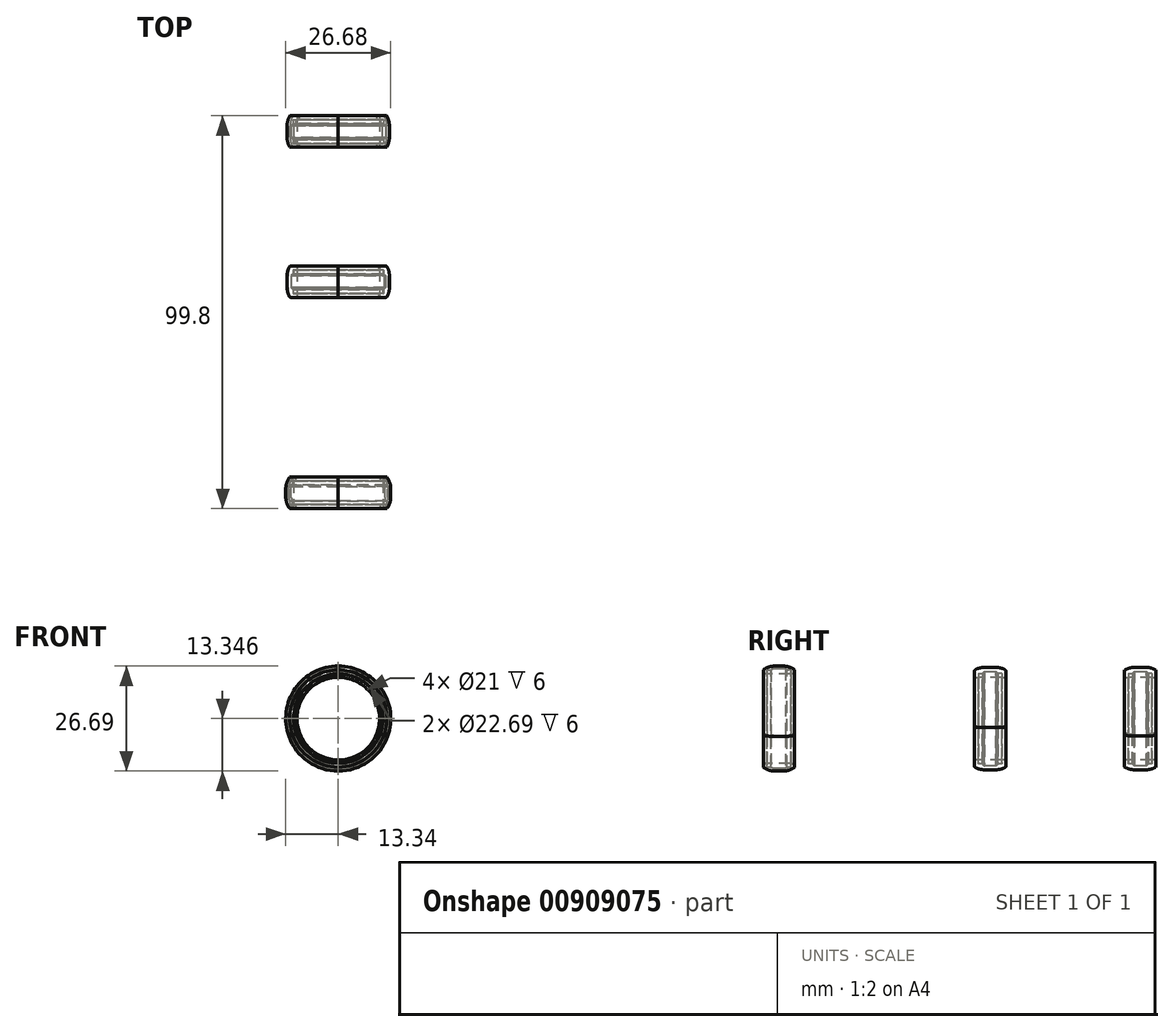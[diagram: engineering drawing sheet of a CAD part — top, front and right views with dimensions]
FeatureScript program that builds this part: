
annotation { "Feature Type Name" : "Feature", "Feature Type Description" : "" }
export const myFeature = defineFeature(function(context is Context, id is Id, definition is map)
    precondition{}
    {
        {
            var Q0;
            Q0=qCreatedBy(makeId("Right.planeOp"),FACE);
            var sketch = newSketch(context, id + "F0", { "sketchPlane" : qUnion([Q0])});
            skLineSegment(sketch, "E0", {"start": v(-19.63, -18.34) * mm, "end": v(80.37, -18.34) * mm, "construction": true});
            skLineSegment(sketch, "E1", {"start": v(-43.65, -18.34) * mm, "end": v(56.35, -18.34) * mm, "construction": true});
            skLineSegment(sketch, "E2.left", {"start": v(-31.4, -5) * mm, "end": v(-31.4, -7) * mm});
            skLineSegment(sketch, "E2.right", {"start": v(-23.4, -5) * mm, "end": v(-23.4, -6) * mm});
            skLineSegment(sketch, "E3", {"start": v(-30.4, -6) * mm, "end": v(-29.4, -6) * mm});
            skLineSegment(sketch, "E4", {"start": v(-24.4, -6) * mm, "end": v(-25.4, -6) * mm});
            skLineSegment(sketch, "E5", {"start": v(-29.4, -6) * mm, "end": v(-29.05, -5.65) * mm});
            skLineSegment(sketch, "E6", {"start": v(-25.4, -6) * mm, "end": v(-25.75, -5.65) * mm});
            skLineSegment(sketch, "E7", {"start": v(-29.05, -5.65) * mm, "end": v(-25.75, -5.65) * mm});
            skArc(sketch, "E8", {"start": v(-23.4, -5) * mm, "mid": v(-27.4, -4.36) * mm, "end": v(-31.4, -5) * mm});
            skPoint(sketch, "E9", {"position": v(-27.4, -5) * mm});
            skLineSegment(sketch, "E10", {"start": v(-23.4, -6) * mm, "end": v(-23.4, -7) * mm});
            skLineSegment(sketch, "E11", {"start": v(-30.4, -6) * mm, "end": v(-30.4, -7) * mm});
            skLineSegment(sketch, "E12", {"start": v(-24.4, -6) * mm, "end": v(-24.4, -7) * mm});
            skLineSegment(sketch, "E13", {"start": v(-31.4, -5) * mm, "end": v(-23.4, -5) * mm});
            skLineSegment(sketch, "E14", {"start": v(-31.4, -7) * mm, "end": v(-30.4, -7) * mm});
            skLineSegment(sketch, "E15", {"start": v(-24.4, -7) * mm, "end": v(-23.4, -7) * mm});
            skLineSegment(sketch, "E16", {"start": v(-30.4, -7) * mm, "end": v(-24.4, -7) * mm});
            skLineSegment(sketch, "E17.left", {"start": v(60.4, -5.34) * mm, "end": v(60.4, -7.84) * mm});
            skLineSegment(sketch, "E17.right", {"start": v(68.4, -5.34) * mm, "end": v(68.4, -6.84) * mm});
            skLineSegment(sketch, "E18", {"start": v(61.4, -6.84) * mm, "end": v(62.4, -6.84) * mm});
            skLineSegment(sketch, "E19", {"start": v(67.4, -6.84) * mm, "end": v(66.4, -6.84) * mm});
            skLineSegment(sketch, "E20", {"start": v(62.4, -6.84) * mm, "end": v(62.9, -6.34) * mm});
            skLineSegment(sketch, "E21", {"start": v(66.4, -6.84) * mm, "end": v(65.9, -6.34) * mm});
            skLineSegment(sketch, "E22", {"start": v(62.9, -6.34) * mm, "end": v(65.9, -6.34) * mm});
            skArc(sketch, "E23", {"start": v(68.4, -5.34) * mm, "mid": v(64.4, -4.7) * mm, "end": v(60.4, -5.34) * mm});
            skPoint(sketch, "E24", {"position": v(64.4, -5.34) * mm});
            skLineSegment(sketch, "E25", {"start": v(68.4, -6.84) * mm, "end": v(68.4, -7.84) * mm});
            skLineSegment(sketch, "E26", {"start": v(61.4, -6.84) * mm, "end": v(61.4, -7.84) * mm});
            skLineSegment(sketch, "E27", {"start": v(67.4, -6.84) * mm, "end": v(67.4, -7.84) * mm});
            skLineSegment(sketch, "E28", {"start": v(60.4, -5.34) * mm, "end": v(68.4, -5.34) * mm});
            skLineSegment(sketch, "E29", {"start": v(60.4, -7.84) * mm, "end": v(61.4, -7.84) * mm});
            skLineSegment(sketch, "E30", {"start": v(67.4, -7.84) * mm, "end": v(68.4, -7.84) * mm});
            skLineSegment(sketch, "E31", {"start": v(61.4, -7.84) * mm, "end": v(67.4, -7.84) * mm});
            skLineSegment(sketch, "E32.left", {"start": v(-14.14, -5.7) * mm, "end": v(-14.14, -7.84) * mm});
            skLineSegment(sketch, "E32.right", {"start": v(-6.14, -5.7) * mm, "end": v(-6.14, -7.14) * mm});
            skLineSegment(sketch, "E33", {"start": v(-13.14, -7.14) * mm, "end": v(-12.14, -7.14) * mm});
            skLineSegment(sketch, "E34", {"start": v(-7.14, -7.14) * mm, "end": v(-8.14, -7.14) * mm});
            skLineSegment(sketch, "E35", {"start": v(-12.14, -7.14) * mm, "end": v(-11.4, -6.4) * mm});
            skLineSegment(sketch, "E36", {"start": v(-8.14, -7.14) * mm, "end": v(-8.9, -6.4) * mm});
            skLineSegment(sketch, "E37", {"start": v(-11.4, -6.4) * mm, "end": v(-8.9, -6.4) * mm});
            skPoint(sketch, "E38", {"position": v(-10.14, -5.7) * mm});
            skLineSegment(sketch, "E39", {"start": v(-6.14, -7.14) * mm, "end": v(-6.14, -7.84) * mm});
            skLineSegment(sketch, "E40", {"start": v(-13.14, -7.14) * mm, "end": v(-13.14, -7.84) * mm});
            skLineSegment(sketch, "E41", {"start": v(-7.14, -7.14) * mm, "end": v(-7.14, -7.84) * mm});
            skLineSegment(sketch, "E42", {"start": v(-14.14, -5.7) * mm, "end": v(-6.14, -5.7) * mm});
            skLineSegment(sketch, "E43", {"start": v(-14.14, -7.84) * mm, "end": v(-13.14, -7.84) * mm});
            skLineSegment(sketch, "E44", {"start": v(-7.14, -7.84) * mm, "end": v(-6.14, -7.84) * mm});
            skLineSegment(sketch, "E45", {"start": v(-13.14, -7.84) * mm, "end": v(-7.14, -7.84) * mm});
            skLineSegment(sketch, "E46.left", {"start": v(22.26, -5.34) * mm, "end": v(22.26, -7.84) * mm});
            skLineSegment(sketch, "E46.right", {"start": v(30.26, -5.34) * mm, "end": v(30.26, -6.84) * mm});
            skLineSegment(sketch, "E47", {"start": v(23.26, -6.84) * mm, "end": v(24.26, -6.84) * mm});
            skLineSegment(sketch, "E48", {"start": v(29.26, -6.84) * mm, "end": v(28.26, -6.84) * mm});
            skLineSegment(sketch, "E49", {"start": v(24.26, -6.84) * mm, "end": v(24.76, -6.34) * mm});
            skLineSegment(sketch, "E50", {"start": v(28.26, -6.84) * mm, "end": v(27.76, -6.34) * mm});
            skLineSegment(sketch, "E51", {"start": v(24.76, -6.34) * mm, "end": v(27.76, -6.34) * mm});
            skPoint(sketch, "E52", {"position": v(26.26, -5.34) * mm});
            skLineSegment(sketch, "E53", {"start": v(30.26, -6.84) * mm, "end": v(30.26, -7.84) * mm});
            skLineSegment(sketch, "E54", {"start": v(23.26, -6.84) * mm, "end": v(23.26, -7.84) * mm});
            skLineSegment(sketch, "E55", {"start": v(29.26, -6.84) * mm, "end": v(29.26, -7.84) * mm});
            skLineSegment(sketch, "E56", {"start": v(22.26, -5.34) * mm, "end": v(30.26, -5.34) * mm});
            skLineSegment(sketch, "E57", {"start": v(22.26, -7.84) * mm, "end": v(23.26, -7.84) * mm});
            skLineSegment(sketch, "E58", {"start": v(29.26, -7.84) * mm, "end": v(30.26, -7.84) * mm});
            skLineSegment(sketch, "E59", {"start": v(23.26, -7.84) * mm, "end": v(29.26, -7.84) * mm});
            skSolve(sketch);
        }
        {
            var Q0;
            Q0=makeQuery(id+"F0.imprint","IMPRINT",FACE,{"disambiguationData":[TD([[makeQuery(id+"F0.imprint","IMPRINT",EDGE,{"derivedFrom":sQuery(id+"F0.wireOp",EDGE,"E3")}),-1.0]])]});
            var Q1;
            Q1=sQuery(id+"F0.wireOp",EDGE,"E0");
            revolve(context, id + "F1", {"surfaceOperationType" : NewSurfaceOperationType.NEW, "entities" : qUnion([Q0]), "axis" : qUnion([Q1]), "revolveType" : RevolveType.FULL});
        }
        {
            var Q0;
            Q0=makeQuery(id+"F1.opRevolve","SWEPT_EDGE",EDGE,{"disambiguationData":[OSD([sQuery(id+"F0.wireOp",EDGE,"E5"),sQuery(id+"F0.wireOp",EDGE,"E7")])]});
            var Q1;
            Q1=makeQuery(id+"F1.opRevolve","SWEPT_EDGE",EDGE,{"disambiguationData":[OSD([sQuery(id+"F0.wireOp",EDGE,"E6"),sQuery(id+"F0.wireOp",EDGE,"E7")])]});
            fillet(context, id + "F2", {"entities" : qUnion([Q0, Q1]), "radius" : 1 * mm, "tangentPropagation" : true, "allowEdgeOverflow" : false});
        }
        {
            var Q0;
            Q0=makeQuery(id+"F0.imprint","IMPRINT",FACE,{"disambiguationData":[TD([[makeQuery(id+"F0.imprint","IMPRINT",EDGE,{"derivedFrom":sQuery(id+"F0.wireOp",EDGE,"E2.left")}),1.0]])]});
            var Q1;
            Q1=makeQuery(id+"F0.imprint","IMPRINT",FACE,{"disambiguationData":[TD([[makeQuery(id+"F0.imprint","IMPRINT",EDGE,{"derivedFrom":sQuery(id+"F0.wireOp",EDGE,"E17.left")}),1.0]])]});
            var Q2;
            Q2=sQuery(id+"F0.wireOp",EDGE,"E0");
            revolve(context, id + "F3", {"surfaceOperationType" : NewSurfaceOperationType.NEW, "entities" : qUnion([Q0, Q1]), "axis" : qUnion([Q2]), "revolveType" : RevolveType.ONE_DIRECTION, "angle" : 110 * degree});
        }
        {
            var Q0;
            Q0=makeQuery(id+"F3.opRevolve","SWEPT_EDGE",EDGE,{"disambiguationData":[OSD([sQuery(id+"F0.wireOp",EDGE,"E4"),sQuery(id+"F0.wireOp",EDGE,"E6")])]});
            var Q1;
            Q1=makeQuery(id+"F3.opRevolve","SWEPT_EDGE",EDGE,{"disambiguationData":[OSD([sQuery(id+"F0.wireOp",EDGE,"E5"),sQuery(id+"F0.wireOp",EDGE,"E7")])]});
            var Q2;
            Q2=makeQuery(id+"F3.opRevolve","SWEPT_EDGE",EDGE,{"disambiguationData":[OSD([sQuery(id+"F0.wireOp",EDGE,"E2.left"),sQuery(id+"F0.wireOp",EDGE,"E14")])]});
            var Q3;
            Q3=makeQuery(id+"F3.opRevolve","SWEPT_EDGE",EDGE,{"disambiguationData":[OSD([sQuery(id+"F0.wireOp",EDGE,"E10"),sQuery(id+"F0.wireOp",EDGE,"E15")])]});
            fillet(context, id + "F4", {"entities" : qUnion([Q0, Q1, Q2, Q3]), "radius" : 1 * mm, "tangentPropagation" : true, "allowEdgeOverflow" : false});
        }
        {
            var Q0;
            Q0=makeQuery(id+"F0.imprint","IMPRINT",FACE,{"disambiguationData":[TD([[makeQuery(id+"F0.imprint","IMPRINT",EDGE,{"derivedFrom":sQuery(id+"F0.wireOp",EDGE,"E2.left")}),1.0]])]});
            var Q1;
            Q1=makeQuery(id+"F0.imprint","IMPRINT",FACE,{"disambiguationData":[TD([[makeQuery(id+"F0.imprint","IMPRINT",EDGE,{"derivedFrom":sQuery(id+"F0.wireOp",EDGE,"E17.left")}),1.0]])]});
            var Q2;
            Q2=sQuery(id+"F0.wireOp",EDGE,"E0");
            revolve(context, id + "F5", {"surfaceOperationType" : NewSurfaceOperationType.NEW, "entities" : qUnion([Q0, Q1]), "axis" : qUnion([Q2]), "revolveType" : RevolveType.TWO_DIRECTIONS, "angle" : 250 * degree, "angleBack" : 110 * degree});
        }
        {
            var Q0;
            Q0=makeQuery(id+"F5.opRevolve","SWEPT_EDGE",EDGE,{"disambiguationData":[OSD([sQuery(id+"F0.wireOp",EDGE,"E4"),sQuery(id+"F0.wireOp",EDGE,"E6")])]});
            var Q1;
            Q1=makeQuery(id+"F5.opRevolve","SWEPT_EDGE",EDGE,{"disambiguationData":[OSD([sQuery(id+"F0.wireOp",EDGE,"E10"),sQuery(id+"F0.wireOp",EDGE,"E15")])]});
            var Q2;
            Q2=makeQuery(id+"F5.opRevolve","SWEPT_EDGE",EDGE,{"disambiguationData":[OSD([sQuery(id+"F0.wireOp",EDGE,"E2.left"),sQuery(id+"F0.wireOp",EDGE,"E14")])]});
            var Q3;
            Q3=makeQuery(id+"F5.opRevolve","SWEPT_EDGE",EDGE,{"disambiguationData":[OSD([sQuery(id+"F0.wireOp",EDGE,"E5"),sQuery(id+"F0.wireOp",EDGE,"E7")])]});
            fillet(context, id + "F6", {"entities" : qUnion([Q0, Q1, Q2, Q3]), "radius" : 1 * mm, "tangentPropagation" : true, "allowEdgeOverflow" : false});
        }
        {
            var Q0;
            Q0=makeQuery(id+"F0.imprint","IMPRINT",FACE,{"disambiguationData":[TD([[makeQuery(id+"F0.imprint","IMPRINT",EDGE,{"derivedFrom":sQuery(id+"F0.wireOp",EDGE,"E2.left")}),1.0]])]});
            var Q1;
            Q1=makeQuery(id+"F0.imprint","IMPRINT",FACE,{"disambiguationData":[TD([[makeQuery(id+"F0.imprint","IMPRINT",EDGE,{"derivedFrom":sQuery(id+"F0.wireOp",EDGE,"E17.left")}),1.0]])]});
            var Q2;
            Q2=sQuery(id+"F0.wireOp",EDGE,"E0");
            revolve(context, id + "F7", {"surfaceOperationType" : NewSurfaceOperationType.NEW, "entities" : qUnion([Q0, Q1]), "axis" : qUnion([Q2]), "revolveType" : RevolveType.TWO_DIRECTIONS, "angle" : 360 * degree, "angleBack" : 250 * degree});
        }
        {
            var Q0;
            Q0=makeQuery(id+"F7.opRevolve","SWEPT_EDGE",EDGE,{"disambiguationData":[OSD([sQuery(id+"F0.wireOp",EDGE,"E5"),sQuery(id+"F0.wireOp",EDGE,"E7")])]});
            var Q1;
            Q1=makeQuery(id+"F7.opRevolve","SWEPT_EDGE",EDGE,{"disambiguationData":[OSD([sQuery(id+"F0.wireOp",EDGE,"E2.left"),sQuery(id+"F0.wireOp",EDGE,"E14")])]});
            var Q2;
            Q2=makeQuery(id+"F7.opRevolve","SWEPT_EDGE",EDGE,{"disambiguationData":[OSD([sQuery(id+"F0.wireOp",EDGE,"E10"),sQuery(id+"F0.wireOp",EDGE,"E15")])]});
            var Q3;
            Q3=makeQuery(id+"F7.opRevolve","SWEPT_EDGE",EDGE,{"disambiguationData":[OSD([sQuery(id+"F0.wireOp",EDGE,"E4"),sQuery(id+"F0.wireOp",EDGE,"E6")])]});
            fillet(context, id + "F8", {"entities" : qUnion([Q0, Q1, Q2, Q3]), "radius" : 1 * mm, "tangentPropagation" : true, "allowEdgeOverflow" : false});
        }
        {
            var Q0;
            Q0=makeQuery(id+"F5.opRevolve","SWEPT_EDGE",EDGE,{"disambiguationData":[OSD([sQuery(id+"F0.wireOp",EDGE,"E2.right"),sQuery(id+"F0.wireOp",EDGE,"E8"),sQuery(id+"F0.wireOp",EDGE,"E13")])]});
            var Q1;
            Q1=makeQuery(id+"F5.opRevolve","SWEPT_EDGE",EDGE,{"disambiguationData":[OSD([sQuery(id+"F0.wireOp",EDGE,"E2.left"),sQuery(id+"F0.wireOp",EDGE,"E8"),sQuery(id+"F0.wireOp",EDGE,"E13")])]});
            var Q2;
            Q2=makeQuery(id+"F7.opRevolve","SWEPT_EDGE",EDGE,{"disambiguationData":[OSD([sQuery(id+"F0.wireOp",EDGE,"E2.left"),sQuery(id+"F0.wireOp",EDGE,"E8"),sQuery(id+"F0.wireOp",EDGE,"E13")])]});
            var Q3;
            Q3=makeQuery(id+"F7.opRevolve","SWEPT_EDGE",EDGE,{"disambiguationData":[OSD([sQuery(id+"F0.wireOp",EDGE,"E2.right"),sQuery(id+"F0.wireOp",EDGE,"E8"),sQuery(id+"F0.wireOp",EDGE,"E13")])]});
            var Q4;
            Q4=makeQuery(id+"F3.opRevolve","SWEPT_EDGE",EDGE,{"disambiguationData":[OSD([sQuery(id+"F0.wireOp",EDGE,"E2.right"),sQuery(id+"F0.wireOp",EDGE,"E8"),sQuery(id+"F0.wireOp",EDGE,"E13")])]});
            var Q5;
            Q5=makeQuery(id+"F3.opRevolve","SWEPT_EDGE",EDGE,{"disambiguationData":[OSD([sQuery(id+"F0.wireOp",EDGE,"E2.left"),sQuery(id+"F0.wireOp",EDGE,"E8"),sQuery(id+"F0.wireOp",EDGE,"E13")])]});
            fillet(context, id + "F9", {"entities" : qUnion([Q0, Q1, Q2, Q3, Q4, Q5]), "radius" : 5 * mm, "tangentPropagation" : true, "allowEdgeOverflow" : false});
        }
        {
            var Q0;
            Q0=makeQuery(id+"F0.imprint","IMPRINT",FACE,{"disambiguationData":[TD([[makeQuery(id+"F0.imprint","IMPRINT",EDGE,{"derivedFrom":sQuery(id+"F0.wireOp",EDGE,"E18")}),-1.0]])]});
            var Q1;
            Q1=sQuery(id+"F0.wireOp",EDGE,"E1");
            revolve(context, id + "F10", {"surfaceOperationType" : NewSurfaceOperationType.NEW, "entities" : qUnion([Q0]), "axis" : qUnion([Q1]), "revolveType" : RevolveType.FULL});
        }
        {
            var Q0;
            Q0=makeQuery(id+"F3.opRevolve","SWEPT_EDGE",EDGE,{"disambiguationData":[OSD([sQuery(id+"F0.wireOp",EDGE,"E17.right"),sQuery(id+"F0.wireOp",EDGE,"E23"),sQuery(id+"F0.wireOp",EDGE,"E28")])]});
            var Q1;
            Q1=makeQuery(id+"F3.opRevolve","SWEPT_EDGE",EDGE,{"disambiguationData":[OSD([sQuery(id+"F0.wireOp",EDGE,"E17.left"),sQuery(id+"F0.wireOp",EDGE,"E23"),sQuery(id+"F0.wireOp",EDGE,"E28")])]});
            var Q2;
            Q2=makeQuery(id+"F5.opRevolve","SWEPT_EDGE",EDGE,{"disambiguationData":[OSD([sQuery(id+"F0.wireOp",EDGE,"E17.left"),sQuery(id+"F0.wireOp",EDGE,"E23"),sQuery(id+"F0.wireOp",EDGE,"E28")])]});
            var Q3;
            Q3=makeQuery(id+"F7.opRevolve","SWEPT_EDGE",EDGE,{"disambiguationData":[OSD([sQuery(id+"F0.wireOp",EDGE,"E17.left"),sQuery(id+"F0.wireOp",EDGE,"E23"),sQuery(id+"F0.wireOp",EDGE,"E28")])]});
            var Q4;
            Q4=makeQuery(id+"F5.opRevolve","SWEPT_EDGE",EDGE,{"disambiguationData":[OSD([sQuery(id+"F0.wireOp",EDGE,"E17.right"),sQuery(id+"F0.wireOp",EDGE,"E23"),sQuery(id+"F0.wireOp",EDGE,"E28")])]});
            var Q5;
            Q5=makeQuery(id+"F7.opRevolve","SWEPT_EDGE",EDGE,{"disambiguationData":[OSD([sQuery(id+"F0.wireOp",EDGE,"E17.right"),sQuery(id+"F0.wireOp",EDGE,"E23"),sQuery(id+"F0.wireOp",EDGE,"E28")])]});
            chamfer(context, id + "F11", {"entities" : qUnion([Q0, Q1, Q2, Q3, Q4, Q5]), "width" : 0.7 * mm, "tangentPropagation" : true});
        }
        {
            var Q0;
            {var subQ0=sQuery(id+"F0.wireOp",EDGE,"E28");Q0=makeQuery(id+"F11.opChamfer","BLEND_EDGE",EDGE,{"blendedFrom":[makeQuery(id+"F3.opRevolve","SWEPT_EDGE",EDGE,{"disambiguationData":[OSD([sQuery(id+"F0.wireOp",EDGE,"E17.right"),sQuery(id+"F0.wireOp",EDGE,"E23"),subQ0])]}),makeQuery(id+"F3.opRevolve","SWEPT_FACE",FACE,{"disambiguationData":[OSD([subQ0])]})],"blendedInto":[makeQuery(id+"F3.opRevolve","SWEPT_FACE",FACE,{"disambiguationData":[OSD([subQ0])]})]});}
            var Q1;
            {var subQ0=sQuery(id+"F0.wireOp",EDGE,"E28");Q1=makeQuery(id+"F11.opChamfer","BLEND_EDGE",EDGE,{"blendedFrom":[makeQuery(id+"F3.opRevolve","SWEPT_EDGE",EDGE,{"disambiguationData":[OSD([sQuery(id+"F0.wireOp",EDGE,"E17.left"),sQuery(id+"F0.wireOp",EDGE,"E23"),subQ0])]}),makeQuery(id+"F3.opRevolve","SWEPT_FACE",FACE,{"disambiguationData":[OSD([subQ0])]})],"blendedInto":[makeQuery(id+"F3.opRevolve","SWEPT_FACE",FACE,{"disambiguationData":[OSD([subQ0])]})]});}
            var Q2;
            {var subQ0=sQuery(id+"F0.wireOp",EDGE,"E28");Q2=makeQuery(id+"F11.opChamfer","BLEND_EDGE",EDGE,{"blendedFrom":[makeQuery(id+"F7.opRevolve","SWEPT_EDGE",EDGE,{"disambiguationData":[OSD([sQuery(id+"F0.wireOp",EDGE,"E17.right"),sQuery(id+"F0.wireOp",EDGE,"E23"),subQ0])]}),makeQuery(id+"F7.opRevolve","SWEPT_FACE",FACE,{"disambiguationData":[OSD([subQ0])]})],"blendedInto":[makeQuery(id+"F7.opRevolve","SWEPT_FACE",FACE,{"disambiguationData":[OSD([subQ0])]})]});}
            var Q3;
            {var subQ0=sQuery(id+"F0.wireOp",EDGE,"E28");Q3=makeQuery(id+"F11.opChamfer","BLEND_EDGE",EDGE,{"blendedFrom":[makeQuery(id+"F7.opRevolve","SWEPT_EDGE",EDGE,{"disambiguationData":[OSD([sQuery(id+"F0.wireOp",EDGE,"E17.left"),sQuery(id+"F0.wireOp",EDGE,"E23"),subQ0])]}),makeQuery(id+"F7.opRevolve","SWEPT_FACE",FACE,{"disambiguationData":[OSD([subQ0])]})],"blendedInto":[makeQuery(id+"F7.opRevolve","SWEPT_FACE",FACE,{"disambiguationData":[OSD([subQ0])]})]});}
            var Q4;
            {var subQ0=sQuery(id+"F0.wireOp",EDGE,"E28");Q4=makeQuery(id+"F11.opChamfer","BLEND_EDGE",EDGE,{"blendedFrom":[makeQuery(id+"F5.opRevolve","SWEPT_EDGE",EDGE,{"disambiguationData":[OSD([sQuery(id+"F0.wireOp",EDGE,"E17.left"),sQuery(id+"F0.wireOp",EDGE,"E23"),subQ0])]}),makeQuery(id+"F5.opRevolve","SWEPT_FACE",FACE,{"disambiguationData":[OSD([subQ0])]})],"blendedInto":[makeQuery(id+"F5.opRevolve","SWEPT_FACE",FACE,{"disambiguationData":[OSD([subQ0])]})]});}
            var Q5;
            {var subQ0=sQuery(id+"F0.wireOp",EDGE,"E28");Q5=makeQuery(id+"F11.opChamfer","BLEND_EDGE",EDGE,{"blendedFrom":[makeQuery(id+"F5.opRevolve","SWEPT_EDGE",EDGE,{"disambiguationData":[OSD([sQuery(id+"F0.wireOp",EDGE,"E17.right"),sQuery(id+"F0.wireOp",EDGE,"E23"),subQ0])]}),makeQuery(id+"F5.opRevolve","SWEPT_FACE",FACE,{"disambiguationData":[OSD([subQ0])]})],"blendedInto":[makeQuery(id+"F5.opRevolve","SWEPT_FACE",FACE,{"disambiguationData":[OSD([subQ0])]})]});}
            fillet(context, id + "F12", {"entities" : qUnion([Q0, Q1, Q2, Q3, Q4, Q5]), "radius" : 5 * mm, "tangentPropagation" : true, "allowEdgeOverflow" : false});
        }
        {
            var Q0;
            Q0=makeQuery(id+"F0.imprint","IMPRINT",FACE,{"disambiguationData":[TD([[makeQuery(id+"F0.imprint","IMPRINT",EDGE,{"derivedFrom":sQuery(id+"F0.wireOp",EDGE,"E47")}),-1.0]])]});
            var Q1;
            Q1=sQuery(id+"F0.wireOp",EDGE,"E1");
            revolve(context, id + "F13", {"surfaceOperationType" : NewSurfaceOperationType.NEW, "entities" : qUnion([Q0]), "axis" : qUnion([Q1]), "revolveType" : RevolveType.FULL});
        }
        {
            var Q0;
            Q0=makeQuery(id+"F0.imprint","IMPRINT",FACE,{"disambiguationData":[TD([[makeQuery(id+"F0.imprint","IMPRINT",EDGE,{"derivedFrom":sQuery(id+"F0.wireOp",EDGE,"E46.left")}),1.0]])]});
            var Q1;
            Q1=sQuery(id+"F0.wireOp",EDGE,"E1");
            revolve(context, id + "F14", {"surfaceOperationType" : NewSurfaceOperationType.NEW, "entities" : qUnion([Q0]), "axis" : qUnion([Q1]), "revolveType" : RevolveType.ONE_DIRECTION, "angle" : 100 * degree});
        }
        {
            var Q0;
            Q0=makeQuery(id+"F0.imprint","IMPRINT",FACE,{"disambiguationData":[TD([[makeQuery(id+"F0.imprint","IMPRINT",EDGE,{"derivedFrom":sQuery(id+"F0.wireOp",EDGE,"E46.left")}),1.0]])]});
            var Q1;
            Q1=sQuery(id+"F0.wireOp",EDGE,"E1");
            revolve(context, id + "F15", {"surfaceOperationType" : NewSurfaceOperationType.NEW, "entities" : qUnion([Q0]), "axis" : qUnion([Q1]), "revolveType" : RevolveType.TWO_DIRECTIONS, "angle" : 260 * degree, "angleBack" : 100 * degree});
        }
        {
            var Q0;
            Q0=makeQuery(id+"F0.imprint","IMPRINT",FACE,{"disambiguationData":[TD([[makeQuery(id+"F0.imprint","IMPRINT",EDGE,{"derivedFrom":sQuery(id+"F0.wireOp",EDGE,"E46.left")}),1.0]])]});
            var Q1;
            Q1=sQuery(id+"F0.wireOp",EDGE,"E1");
            revolve(context, id + "F16", {"surfaceOperationType" : NewSurfaceOperationType.NEW, "entities" : qUnion([Q0]), "axis" : qUnion([Q1]), "revolveType" : RevolveType.TWO_DIRECTIONS, "angle" : 360 * degree, "angleBack" : 260 * degree});
        }
        {
            var Q0;
            Q0=makeQuery(id+"F14.opRevolve","SWEPT_EDGE",EDGE,{"disambiguationData":[OSD([sQuery(id+"F0.wireOp",EDGE,"E46.right"),sQuery(id+"F0.wireOp",EDGE,"E56")])]});
            var Q1;
            Q1=makeQuery(id+"F16.opRevolve","SWEPT_EDGE",EDGE,{"disambiguationData":[OSD([sQuery(id+"F0.wireOp",EDGE,"E46.right"),sQuery(id+"F0.wireOp",EDGE,"E56")])]});
            var Q2;
            Q2=makeQuery(id+"F15.opRevolve","SWEPT_EDGE",EDGE,{"disambiguationData":[OSD([sQuery(id+"F0.wireOp",EDGE,"E46.right"),sQuery(id+"F0.wireOp",EDGE,"E56")])]});
            var Q3;
            Q3=makeQuery(id+"F14.opRevolve","SWEPT_EDGE",EDGE,{"disambiguationData":[OSD([sQuery(id+"F0.wireOp",EDGE,"E46.left"),sQuery(id+"F0.wireOp",EDGE,"E56")])]});
            var Q4;
            Q4=makeQuery(id+"F15.opRevolve","SWEPT_EDGE",EDGE,{"disambiguationData":[OSD([sQuery(id+"F0.wireOp",EDGE,"E46.left"),sQuery(id+"F0.wireOp",EDGE,"E56")])]});
            var Q5;
            Q5=makeQuery(id+"F16.opRevolve","SWEPT_EDGE",EDGE,{"disambiguationData":[OSD([sQuery(id+"F0.wireOp",EDGE,"E46.left"),sQuery(id+"F0.wireOp",EDGE,"E56")])]});
            chamfer(context, id + "F17", {"entities" : qUnion([Q0, Q1, Q2, Q3, Q4, Q5]), "width" : .7 * mm, "tangentPropagation" : true});
        }
        {
            var Q0;
            {var subQ0=sQuery(id+"F0.wireOp",EDGE,"E56");Q0=makeQuery(id+"F17.opChamfer","BLEND_EDGE",EDGE,{"blendedFrom":[makeQuery(id+"F14.opRevolve","SWEPT_EDGE",EDGE,{"disambiguationData":[OSD([sQuery(id+"F0.wireOp",EDGE,"E46.left"),subQ0])]}),makeQuery(id+"F14.opRevolve","SWEPT_FACE",FACE,{"disambiguationData":[OSD([subQ0])]})],"blendedInto":[makeQuery(id+"F14.opRevolve","SWEPT_FACE",FACE,{"disambiguationData":[OSD([subQ0])]})]});}
            var Q1;
            {var subQ0=sQuery(id+"F0.wireOp",EDGE,"E56");Q1=makeQuery(id+"F17.opChamfer","BLEND_EDGE",EDGE,{"blendedFrom":[makeQuery(id+"F16.opRevolve","SWEPT_EDGE",EDGE,{"disambiguationData":[OSD([sQuery(id+"F0.wireOp",EDGE,"E46.left"),subQ0])]}),makeQuery(id+"F16.opRevolve","SWEPT_FACE",FACE,{"disambiguationData":[OSD([subQ0])]})],"blendedInto":[makeQuery(id+"F16.opRevolve","SWEPT_FACE",FACE,{"disambiguationData":[OSD([subQ0])]})]});}
            var Q2;
            {var subQ0=sQuery(id+"F0.wireOp",EDGE,"E56");Q2=makeQuery(id+"F17.opChamfer","BLEND_EDGE",EDGE,{"blendedFrom":[makeQuery(id+"F16.opRevolve","SWEPT_EDGE",EDGE,{"disambiguationData":[OSD([sQuery(id+"F0.wireOp",EDGE,"E46.right"),subQ0])]}),makeQuery(id+"F16.opRevolve","SWEPT_FACE",FACE,{"disambiguationData":[OSD([subQ0])]})],"blendedInto":[makeQuery(id+"F16.opRevolve","SWEPT_FACE",FACE,{"disambiguationData":[OSD([subQ0])]})]});}
            var Q3;
            {var subQ0=sQuery(id+"F0.wireOp",EDGE,"E56");Q3=makeQuery(id+"F17.opChamfer","BLEND_EDGE",EDGE,{"blendedFrom":[makeQuery(id+"F14.opRevolve","SWEPT_EDGE",EDGE,{"disambiguationData":[OSD([sQuery(id+"F0.wireOp",EDGE,"E46.right"),subQ0])]}),makeQuery(id+"F14.opRevolve","SWEPT_FACE",FACE,{"disambiguationData":[OSD([subQ0])]})],"blendedInto":[makeQuery(id+"F14.opRevolve","SWEPT_FACE",FACE,{"disambiguationData":[OSD([subQ0])]})]});}
            var Q4;
            {var subQ0=sQuery(id+"F0.wireOp",EDGE,"E56");Q4=makeQuery(id+"F17.opChamfer","BLEND_EDGE",EDGE,{"blendedFrom":[makeQuery(id+"F15.opRevolve","SWEPT_EDGE",EDGE,{"disambiguationData":[OSD([sQuery(id+"F0.wireOp",EDGE,"E46.right"),subQ0])]}),makeQuery(id+"F15.opRevolve","SWEPT_FACE",FACE,{"disambiguationData":[OSD([subQ0])]})],"blendedInto":[makeQuery(id+"F15.opRevolve","SWEPT_FACE",FACE,{"disambiguationData":[OSD([subQ0])]})]});}
            var Q5;
            {var subQ0=sQuery(id+"F0.wireOp",EDGE,"E56");Q5=makeQuery(id+"F17.opChamfer","BLEND_EDGE",EDGE,{"blendedFrom":[makeQuery(id+"F15.opRevolve","SWEPT_EDGE",EDGE,{"disambiguationData":[OSD([sQuery(id+"F0.wireOp",EDGE,"E46.left"),subQ0])]}),makeQuery(id+"F15.opRevolve","SWEPT_FACE",FACE,{"disambiguationData":[OSD([subQ0])]})],"blendedInto":[makeQuery(id+"F15.opRevolve","SWEPT_FACE",FACE,{"disambiguationData":[OSD([subQ0])]})]});}
            fillet(context, id + "F18", {"entities" : qUnion([Q0, Q1, Q2, Q3, Q4, Q5]), "radius" : 5 * mm, "tangentPropagation" : true, "allowEdgeOverflow" : false});
        }
        {
            var Q0;
            Q0=makeQuery(id+"F14.opRevolve","SWEPT_EDGE",EDGE,{"disambiguationData":[OSD([sQuery(id+"F0.wireOp",EDGE,"E53"),sQuery(id+"F0.wireOp",EDGE,"E58")])]});
            var Q1;
            Q1=makeQuery(id+"F15.opRevolve","SWEPT_EDGE",EDGE,{"disambiguationData":[OSD([sQuery(id+"F0.wireOp",EDGE,"E53"),sQuery(id+"F0.wireOp",EDGE,"E58")])]});
            var Q2;
            Q2=makeQuery(id+"F16.opRevolve","SWEPT_EDGE",EDGE,{"disambiguationData":[OSD([sQuery(id+"F0.wireOp",EDGE,"E53"),sQuery(id+"F0.wireOp",EDGE,"E58")])]});
            var Q3;
            Q3=makeQuery(id+"F14.opRevolve","SWEPT_EDGE",EDGE,{"disambiguationData":[OSD([sQuery(id+"F0.wireOp",EDGE,"E46.left"),sQuery(id+"F0.wireOp",EDGE,"E57")])]});
            var Q4;
            Q4=makeQuery(id+"F15.opRevolve","SWEPT_EDGE",EDGE,{"disambiguationData":[OSD([sQuery(id+"F0.wireOp",EDGE,"E46.left"),sQuery(id+"F0.wireOp",EDGE,"E57")])]});
            var Q5;
            Q5=makeQuery(id+"F16.opRevolve","SWEPT_EDGE",EDGE,{"disambiguationData":[OSD([sQuery(id+"F0.wireOp",EDGE,"E46.left"),sQuery(id+"F0.wireOp",EDGE,"E57")])]});
            fillet(context, id + "F19", {"entities" : qUnion([Q0, Q1, Q2, Q3, Q4, Q5]), "radius" : 0.35 * mm, "tangentPropagation" : true, "allowEdgeOverflow" : false});
        }
        {
            var Q0;
            {var subQ0=sQuery(id+"F0.wireOp",EDGE,"E46.right");var subQ1=sQuery(id+"F0.wireOp",EDGE,"E56");Q0=makeQuery(id+"F18.opFillet","BLEND_EDGE",EDGE,{"blendedFrom":[makeQuery(id+"F17.opChamfer","BLEND_EDGE",EDGE,{"blendedFrom":[makeQuery(id+"F16.opRevolve","SWEPT_EDGE",EDGE,{"disambiguationData":[OSD([subQ0,subQ1])]}),makeQuery(id+"F16.opRevolve","SWEPT_FACE",FACE,{"disambiguationData":[OSD([subQ1])]})],"blendedInto":[makeQuery(id+"F16.opRevolve","SWEPT_FACE",FACE,{"disambiguationData":[OSD([subQ1])]})]}),makeQuery(id+"F16.opRevolve","SWEPT_FACE",FACE,{"disambiguationData":[OSD([subQ0,sQuery(id+"F0.wireOp",EDGE,"E53")])]})],"blendedInto":[makeQuery(id+"F16.opRevolve","SWEPT_FACE",FACE,{"disambiguationData":[OSD([subQ0,sQuery(id+"F0.wireOp",EDGE,"E53")])]})]});}
            var Q1;
            {var subQ0=sQuery(id+"F0.wireOp",EDGE,"E46.right");var subQ1=sQuery(id+"F0.wireOp",EDGE,"E56");Q1=makeQuery(id+"F18.opFillet","BLEND_EDGE",EDGE,{"blendedFrom":[makeQuery(id+"F17.opChamfer","BLEND_EDGE",EDGE,{"blendedFrom":[makeQuery(id+"F14.opRevolve","SWEPT_EDGE",EDGE,{"disambiguationData":[OSD([subQ0,subQ1])]}),makeQuery(id+"F14.opRevolve","SWEPT_FACE",FACE,{"disambiguationData":[OSD([subQ1])]})],"blendedInto":[makeQuery(id+"F14.opRevolve","SWEPT_FACE",FACE,{"disambiguationData":[OSD([subQ1])]})]}),makeQuery(id+"F14.opRevolve","SWEPT_FACE",FACE,{"disambiguationData":[OSD([subQ0,sQuery(id+"F0.wireOp",EDGE,"E53")])]})],"blendedInto":[makeQuery(id+"F14.opRevolve","SWEPT_FACE",FACE,{"disambiguationData":[OSD([subQ0,sQuery(id+"F0.wireOp",EDGE,"E53")])]})]});}
            var Q2;
            {var subQ0=sQuery(id+"F0.wireOp",EDGE,"E46.right");var subQ1=sQuery(id+"F0.wireOp",EDGE,"E56");Q2=makeQuery(id+"F18.opFillet","BLEND_EDGE",EDGE,{"blendedFrom":[makeQuery(id+"F17.opChamfer","BLEND_EDGE",EDGE,{"blendedFrom":[makeQuery(id+"F15.opRevolve","SWEPT_EDGE",EDGE,{"disambiguationData":[OSD([subQ0,subQ1])]}),makeQuery(id+"F15.opRevolve","SWEPT_FACE",FACE,{"disambiguationData":[OSD([subQ1])]})],"blendedInto":[makeQuery(id+"F15.opRevolve","SWEPT_FACE",FACE,{"disambiguationData":[OSD([subQ1])]})]}),makeQuery(id+"F15.opRevolve","SWEPT_FACE",FACE,{"disambiguationData":[OSD([subQ0,sQuery(id+"F0.wireOp",EDGE,"E53")])]})],"blendedInto":[makeQuery(id+"F15.opRevolve","SWEPT_FACE",FACE,{"disambiguationData":[OSD([subQ0,sQuery(id+"F0.wireOp",EDGE,"E53")])]})]});}
            var Q3;
            {var subQ0=sQuery(id+"F0.wireOp",EDGE,"E46.left");var subQ1=sQuery(id+"F0.wireOp",EDGE,"E56");Q3=makeQuery(id+"F18.opFillet","BLEND_EDGE",EDGE,{"blendedFrom":[makeQuery(id+"F17.opChamfer","BLEND_EDGE",EDGE,{"blendedFrom":[makeQuery(id+"F16.opRevolve","SWEPT_EDGE",EDGE,{"disambiguationData":[OSD([subQ0,subQ1])]}),makeQuery(id+"F16.opRevolve","SWEPT_FACE",FACE,{"disambiguationData":[OSD([subQ1])]})],"blendedInto":[makeQuery(id+"F16.opRevolve","SWEPT_FACE",FACE,{"disambiguationData":[OSD([subQ1])]})]}),makeQuery(id+"F16.opRevolve","SWEPT_FACE",FACE,{"disambiguationData":[OSD([subQ0])]})],"blendedInto":[makeQuery(id+"F16.opRevolve","SWEPT_FACE",FACE,{"disambiguationData":[OSD([subQ0])]})]});}
            var Q4;
            {var subQ0=sQuery(id+"F0.wireOp",EDGE,"E46.left");var subQ1=sQuery(id+"F0.wireOp",EDGE,"E56");Q4=makeQuery(id+"F18.opFillet","BLEND_EDGE",EDGE,{"blendedFrom":[makeQuery(id+"F17.opChamfer","BLEND_EDGE",EDGE,{"blendedFrom":[makeQuery(id+"F14.opRevolve","SWEPT_EDGE",EDGE,{"disambiguationData":[OSD([subQ0,subQ1])]}),makeQuery(id+"F14.opRevolve","SWEPT_FACE",FACE,{"disambiguationData":[OSD([subQ1])]})],"blendedInto":[makeQuery(id+"F14.opRevolve","SWEPT_FACE",FACE,{"disambiguationData":[OSD([subQ1])]})]}),makeQuery(id+"F14.opRevolve","SWEPT_FACE",FACE,{"disambiguationData":[OSD([subQ0])]})],"blendedInto":[makeQuery(id+"F14.opRevolve","SWEPT_FACE",FACE,{"disambiguationData":[OSD([subQ0])]})]});}
            var Q5;
            {var subQ0=sQuery(id+"F0.wireOp",EDGE,"E46.left");var subQ1=sQuery(id+"F0.wireOp",EDGE,"E56");Q5=makeQuery(id+"F18.opFillet","BLEND_EDGE",EDGE,{"blendedFrom":[makeQuery(id+"F17.opChamfer","BLEND_EDGE",EDGE,{"blendedFrom":[makeQuery(id+"F15.opRevolve","SWEPT_EDGE",EDGE,{"disambiguationData":[OSD([subQ0,subQ1])]}),makeQuery(id+"F15.opRevolve","SWEPT_FACE",FACE,{"disambiguationData":[OSD([subQ1])]})],"blendedInto":[makeQuery(id+"F15.opRevolve","SWEPT_FACE",FACE,{"disambiguationData":[OSD([subQ1])]})]}),makeQuery(id+"F15.opRevolve","SWEPT_FACE",FACE,{"disambiguationData":[OSD([subQ0])]})],"blendedInto":[makeQuery(id+"F15.opRevolve","SWEPT_FACE",FACE,{"disambiguationData":[OSD([subQ0])]})]});}
            fillet(context, id + "F20", {"entities" : qUnion([Q0, Q1, Q2, Q3, Q4, Q5]), "radius" : 0.5 * mm, "tangentPropagation" : true, "allowEdgeOverflow" : false});
        }
    });
